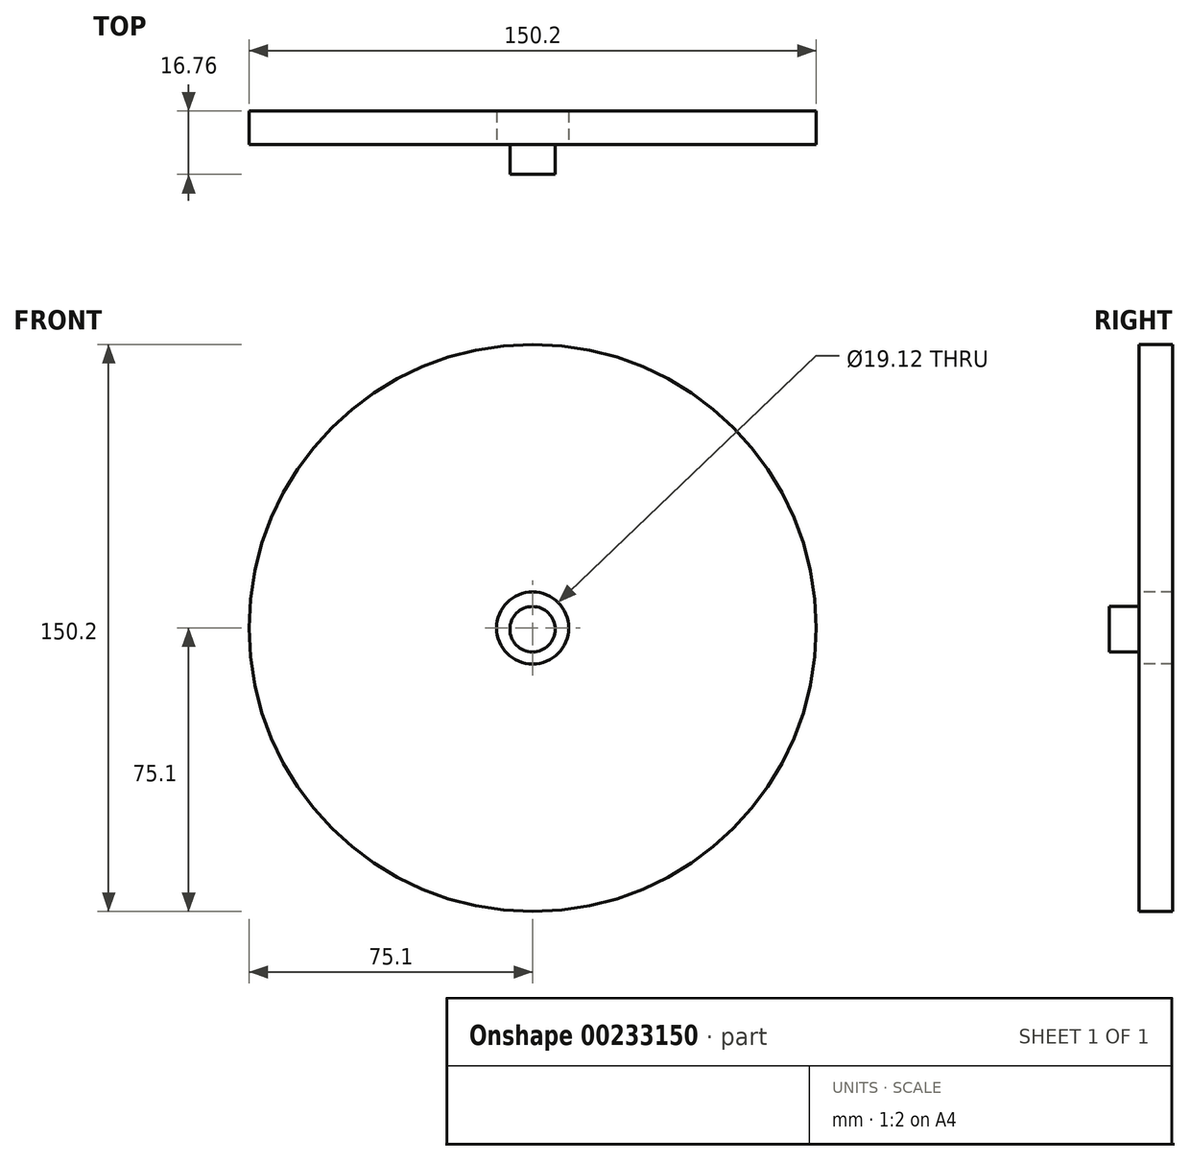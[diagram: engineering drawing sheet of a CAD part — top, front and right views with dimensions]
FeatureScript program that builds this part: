
annotation { "Feature Type Name" : "Feature", "Feature Type Description" : "" }
export const myFeature = defineFeature(function(context is Context, id is Id, definition is map)
    precondition{}
    {
        {
            var Q0;
            Q0=qCreatedBy(makeId("Front.planeOp"),FACE);
            var sketch = newSketch(context, id + "F0", { "sketchPlane" : qUnion([Q0])});
            skCircle(sketch, "E0", {"center": v(0, 0) * mm, "radius": 75.1 * mm});
            skCircle(sketch, "E1", {"center": v(0, 0) * mm, "radius": 7.11 * mm});
            skCircle(sketch, "E2", {"center": v(0, 0) * mm, "radius": 7.21 * mm});
            skCircle(sketch, "E3", {"center": v(0, 0) * mm, "radius": 9.56 * mm});
            skCircle(sketch, "E4", {"center": v(0.22, -0.14) * mm, "radius": 4.7 * mm});
            skPoint(sketch, "E4.first.point", {"position": v(-3.34, 2.9) * mm});
            skPoint(sketch, "E4.second.point", {"position": v(3.3, -3.7) * mm});
            skPoint(sketch, "E4.third.point", {"position": v(-4.23, -1.63) * mm});
            skSolve(sketch);
        }
        {
            var Q0;
            Q0=qCreatedBy(makeId("Front.planeOp"),FACE);
            var sketch = newSketch(context, id + "F1", { "sketchPlane" : qUnion([Q0])});
            skLineSegment(sketch, "E5", {"start": v(0, 9.52) * mm, "end": v(0, 75.46) * mm});
            skLineSegment(sketch, "E6.1.0", {"start": v(-8.24, -4.76) * mm, "end": v(-65.35, -37.73) * mm});
            skLineSegment(sketch, "E6.2.0", {"start": v(8.24, -4.76) * mm, "end": v(65.35, -37.73) * mm});
            skPoint(sketch, "E6.center", {"position": v(0, 0) * mm});
            skLineSegment(sketch, "E7", {"start": v(9.52, 0) * mm, "end": v(75.25, 0) * mm});
            skLineSegment(sketch, "E8.1.0", {"start": v(-4.76, 8.24) * mm, "end": v(-37.63, 65.17) * mm});
            skLineSegment(sketch, "E8.2.0", {"start": v(-4.76, -8.24) * mm, "end": v(-37.63, -65.17) * mm});
            skLineSegment(sketch, "E9", {"start": v(0, -9.52) * mm, "end": v(0, -74.63) * mm});
            skLineSegment(sketch, "E10.1.0", {"start": v(8.24, 4.76) * mm, "end": v(64.64, 37.32) * mm});
            skLineSegment(sketch, "E10.2.0", {"start": v(-8.24, 4.76) * mm, "end": v(-64.64, 37.32) * mm});
            skLineSegment(sketch, "E11", {"start": v(-9.52, 0) * mm, "end": v(-74.43, 0) * mm});
            skLineSegment(sketch, "E12.1.0", {"start": v(4.76, -8.24) * mm, "end": v(37.21, -64.46) * mm});
            skLineSegment(sketch, "E12.2.0", {"start": v(4.76, 8.24) * mm, "end": v(37.21, 64.46) * mm});
            skLineSegment(sketch, "E13", {"start": v(17.37, 72.98) * mm, "end": v(2.6, 9.16) * mm});
            skLineSegment(sketch, "E14.1.0", {"start": v(-71.89, -21.45) * mm, "end": v(-9.23, -2.33) * mm});
            skLineSegment(sketch, "E14.2.0", {"start": v(54.52, -51.53) * mm, "end": v(6.64, -6.83) * mm});
            skLineSegment(sketch, "E15", {"start": v(-9.23, 2.35) * mm, "end": v(-72.36, 17.78) * mm});
            skLineSegment(sketch, "E16.1.0", {"start": v(2.58, -9.16) * mm, "end": v(20.78, -71.56) * mm});
            skLineSegment(sketch, "E16.2.0", {"start": v(6.65, 6.82) * mm, "end": v(51.58, 53.78) * mm});
            skLineSegment(sketch, "E17", {"start": v(9.26, -2.19) * mm, "end": v(71.74, -20.47) * mm});
            skLineSegment(sketch, "E18.1.0", {"start": v(-2.74, 9.12) * mm, "end": v(-18.14, 72.36) * mm});
            skLineSegment(sketch, "E18.2.0", {"start": v(-6.53, -6.93) * mm, "end": v(-53.6, -51.9) * mm});
            skLineSegment(sketch, "E19", {"start": v(72.77, 17.57) * mm, "end": v(9.28, 2.1) * mm});
            skLineSegment(sketch, "E20", {"start": v(-53.55, 52.72) * mm, "end": v(-6.1, 7.31) * mm});
            skLineSegment(sketch, "E21", {"start": v(-20.05, -72.36) * mm, "end": v(-2.8, -9.1) * mm});
            skCircle(sketch, "E22", {"center": v(0, 0) * mm, "radius": 9.52 * mm});
            skPoint(sketch, "E23.orphan", {"position": v(-2.29, 7.27) * mm});
            skPoint(sketch, "E24.orphan", {"position": v(-3.72, 6.45) * mm});
            skPoint(sketch, "E25.orphan", {"position": v(-5.18, 6.45) * mm});
            skPoint(sketch, "E26.orphan", {"position": v(1.86, 6) * mm});
            skPoint(sketch, "E27.orphan", {"position": v(0, 7.03) * mm});
            skPoint(sketch, "E28.orphan", {"position": v(3.62, 6.27) * mm});
            skPoint(sketch, "E29.orphan", {"position": v(5.23, 5.34) * mm});
            skPoint(sketch, "E30.orphan", {"position": v(6.8, 3.93) * mm});
            skPoint(sketch, "E31.orphan", {"position": v(6.8, 1.5) * mm});
            skPoint(sketch, "E32.orphan", {"position": v(7.44, 0) * mm});
            skPoint(sketch, "E33.orphan", {"position": v(7.44, -1.65) * mm});
            skPoint(sketch, "E34.orphan", {"position": v(6.09, -3.51) * mm});
            skPoint(sketch, "E35.orphan", {"position": v(4.26, -4.6) * mm});
            skPoint(sketch, "E36.orphan", {"position": v(3.62, -6.27) * mm});
            skPoint(sketch, "E37.orphan", {"position": v(-6.8, 3.93) * mm});
            skPoint(sketch, "E38.orphan", {"position": v(-7.24, 1.86) * mm});
            skPoint(sketch, "E39.orphan", {"position": v(-7.24, 0) * mm});
            skPoint(sketch, "E40.orphan", {"position": v(-6.12, -1.39) * mm});
            skPoint(sketch, "E41.orphan", {"position": v(-6.09, -3.51) * mm});
            skPoint(sketch, "E42.orphan", {"position": v(-5.15, -5.62) * mm});
            skPoint(sketch, "E43.orphan", {"position": v(-2.07, -6.45) * mm});
            skPoint(sketch, "E44.orphan", {"position": v(-3.72, -6.45) * mm});
            skPoint(sketch, "E45.orphan", {"position": v(0, -7.86) * mm});
            skPoint(sketch, "E46.orphan", {"position": v(2, -7.2) * mm});
            skSolve(sketch);
        }
        {
            var Q0;
            Q0=qCreatedBy(makeId("Front.planeOp"),FACE);
            var sketch = newSketch(context, id + "F2", { "sketchPlane" : qUnion([Q0])});
            skCircle(sketch, "E47", {"center": v(-0.35, -0.18) * mm, "radius": 78.6 * mm});
            skPoint(sketch, "E47.first.point", {"position": v(-35.97, 69.88) * mm});
            skPoint(sketch, "E47.second.point", {"position": v(35.97, -69.88) * mm});
            skPoint(sketch, "E47.third.point", {"position": v(-76.29, -20.47) * mm});
            skSolve(sketch);
        }
        {
            var Q0;
            Q0=sQuery(id+"F1.wireOp",EDGE,"E18.1.0");
            var Q1;
            Q1=sQuery(id+"F1.wireOp",EDGE,"E8.1.0");
            var Q2;
            Q2=sQuery(id+"F1.wireOp",EDGE,"E20");
            var Q3;
            Q3=sQuery(id+"F1.wireOp",EDGE,"E10.2.0");
            var Q4;
            Q4=sQuery(id+"F1.wireOp",EDGE,"E15");
            var Q5;
            Q5=sQuery(id+"F1.wireOp",EDGE,"E11");
            var Q6;
            Q6=sQuery(id+"F1.wireOp",EDGE,"E14.1.0");
            var Q7;
            Q7=sQuery(id+"F1.wireOp",EDGE,"E18.2.0");
            var Q8;
            Q8=sQuery(id+"F1.wireOp",EDGE,"E8.2.0");
            var Q9;
            Q9=sQuery(id+"F1.wireOp",EDGE,"E6.1.0");
            var Q10;
            Q10=sQuery(id+"F1.wireOp",EDGE,"E9");
            var Q11;
            Q11=sQuery(id+"F1.wireOp",EDGE,"E21");
            var Q12;
            Q12=sQuery(id+"F1.wireOp",EDGE,"E16.1.0");
            var Q13;
            Q13=sQuery(id+"F1.wireOp",EDGE,"E12.1.0");
            var Q14;
            Q14=sQuery(id+"F1.wireOp",EDGE,"E14.2.0");
            var Q15;
            Q15=sQuery(id+"F1.wireOp",EDGE,"E6.2.0");
            var Q16;
            Q16=sQuery(id+"F1.wireOp",EDGE,"E17");
            var Q17;
            Q17=sQuery(id+"F1.wireOp",EDGE,"E7");
            var Q18;
            Q18=sQuery(id+"F1.wireOp",EDGE,"E19");
            var Q19;
            Q19=sQuery(id+"F1.wireOp",EDGE,"E10.1.0");
            var Q20;
            Q20=sQuery(id+"F1.wireOp",EDGE,"E16.2.0");
            var Q21;
            Q21=sQuery(id+"F1.wireOp",EDGE,"E12.2.0");
            var Q22;
            Q22=sQuery(id+"F1.wireOp",EDGE,"E13");
            var Q23;
            Q23=sQuery(id+"F1.wireOp",EDGE,"E5");
            extrude(context, id + "F3", {"bodyType" : ToolBodyType.SURFACE, "surfaceEntities" : qUnion([Q0, Q1, Q2, Q3, Q4, Q5, Q6, Q7, Q8, Q9, Q10, Q11, Q12, Q13, Q14, Q15, Q16, Q17, Q18, Q19, Q20, Q21, Q22, Q23]), "depth" : 5.33 * mm});
        }
        {
            var Q0;
            Q0 = qSketchRegion(id + "F0", true);
            extrude(context, id + "F4", {"entities" : qUnion([Q0]), "oppositeDirection" : true, "depth" : 8.9 * mm});
        }
        {
            var Q0;
            Q0=sQuery(id+"F2.wireOp",EDGE,"E47");
            extrude(context, id + "F5", {"bodyType" : ToolBodyType.SURFACE, "surfaceEntities" : qUnion([Q0]), "depth" : 6.86 * mm, "hasSecondDirection" : true, "secondDirectionOppositeDirection" : true, "secondDirectionDepth" : 7.11 * mm});
        }
        {
            var Q0;
            Q0=qCreatedBy(makeId("Front.planeOp"),FACE);
            var sketch = newSketch(context, id + "F6", { "sketchPlane" : qUnion([Q0])});
            skCircle(sketch, "E48", {"center": v(-0.02, -0.33) * mm, "radius": 6.01 * mm});
            skPoint(sketch, "E48.first.point", {"position": v(-2.91, 4.94) * mm});
            skPoint(sketch, "E48.second.point", {"position": v(2.63, -5.73) * mm});
            skPoint(sketch, "E48.third.point", {"position": v(4.55, -4.23) * mm});
            skSolve(sketch);
        }
        {
            var Q0;
            Q0 = qSketchRegion(id + "F6", true);
            extrude(context, id + "F7", {"entities" : qUnion([Q0]), "depth" : 7.87 * mm});
        }
    });
